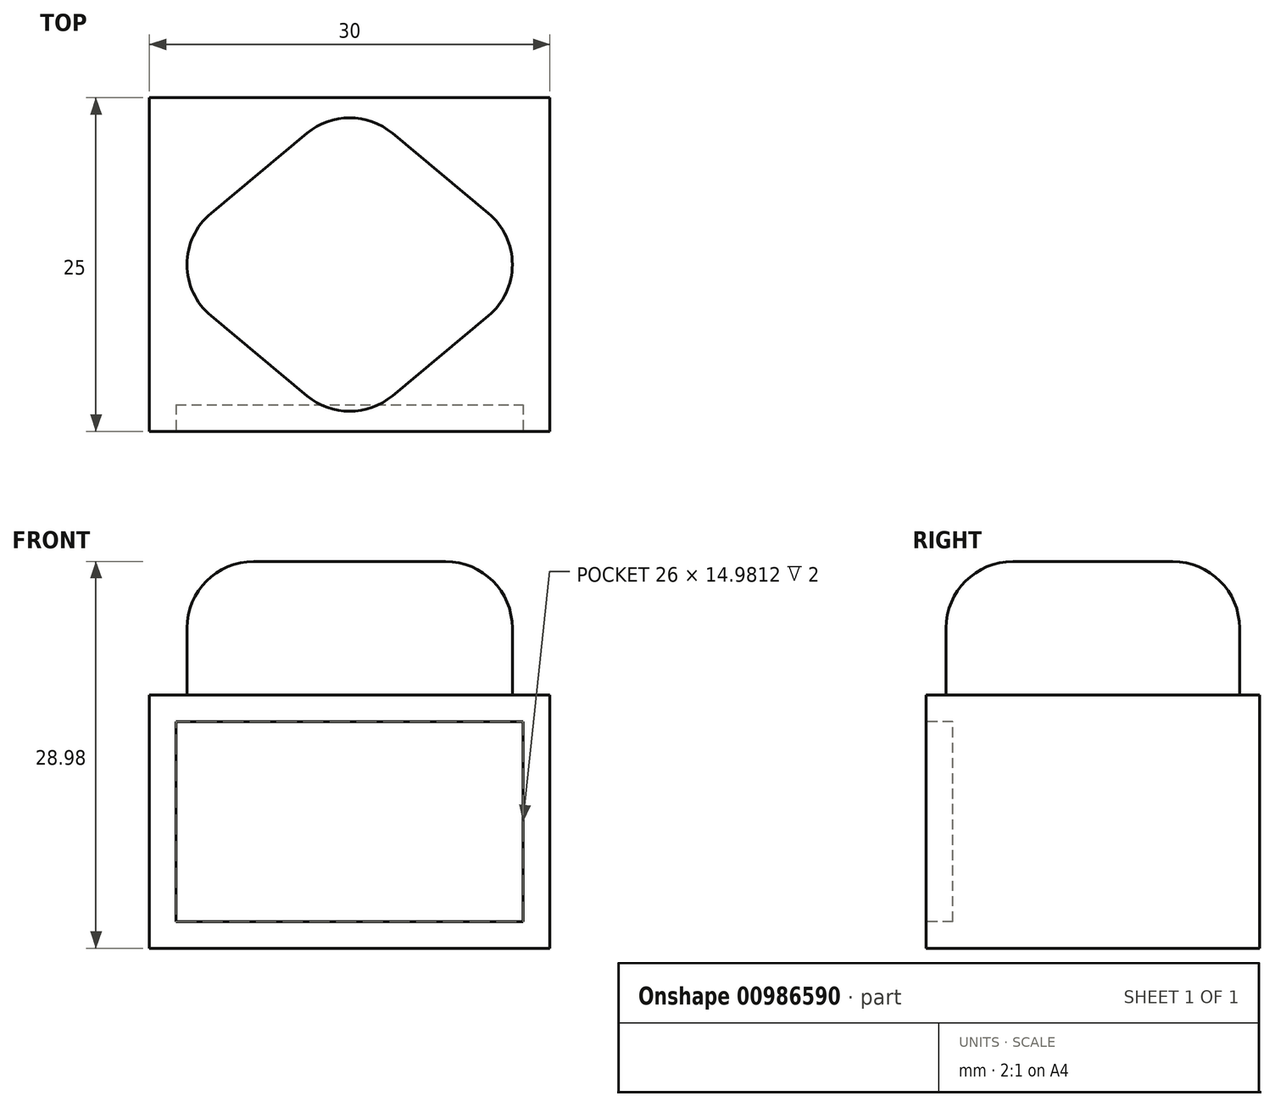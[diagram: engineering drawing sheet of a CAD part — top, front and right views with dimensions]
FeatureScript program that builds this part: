
annotation { "Feature Type Name" : "Feature", "Feature Type Description" : "" }
export const myFeature = defineFeature(function(context is Context, id is Id, definition is map)
    precondition{}
    {
        {
            var Q0;
            Q0=qCreatedBy(makeId("Front.planeOp"),FACE);
            var sketch = newSketch(context, id + "F0", { "sketchPlane" : qUnion([Q0])});
            skLineSegment(sketch, "E0.bottom", {"start": v(0, 0) * mm, "end": v(30, 0) * mm});
            skLineSegment(sketch, "E0.top", {"start": v(0, 18.98) * mm, "end": v(30, 18.98) * mm});
            skLineSegment(sketch, "E0.left", {"start": v(0, 0) * mm, "end": v(0, 18.98) * mm});
            skLineSegment(sketch, "E0.right", {"start": v(30, 0) * mm, "end": v(30, 18.98) * mm});
            skSolve(sketch);
        }
        {
            var Q0;
            Q0 = qSketchRegion(id + "F0", true);
            extrude(context, id + "F1", {"entities" : qUnion([Q0]), "endBound" : BoundingType.SYMMETRIC, "oppositeDirection" : true, "depth" : 25 * mm, "offsetDistance" : 25 * mm});
        }
        {
            var Q0;
            Q0=makeQuery(id+"F1.opExtrude","SWEPT_FACE",FACE,{"disambiguationData":[OSD([sQuery(id+"F0.wireOp",EDGE,"E0.top")])]});
            var sketch = newSketch(context, id + "F2", { "sketchPlane" : qUnion([Q0])});
            skLineSegment(sketch, "E1", {"start": v(0, 0) * mm, "end": v(15, 12.5) * mm});
            skLineSegment(sketch, "E2", {"start": v(15, 12.5) * mm, "end": v(30, 0) * mm});
            skLineSegment(sketch, "E3", {"start": v(30, 0) * mm, "end": v(15, -12.5) * mm});
            skLineSegment(sketch, "E4", {"start": v(15, -12.5) * mm, "end": v(0, 0) * mm});
            skLineSegment(sketch, "E5.0", {"start": v(-3.2, 3.84) * mm, "end": v(11.8, 16.34) * mm});
            skSolve(sketch);
        }
        {
            var Q0;
            Q0 = qSketchRegion(id + "F2", true);
            extrude(context, id + "F3", {"entities" : qUnion([Q0]), "operationType" : NewBodyOperationType.ADD, "depth" : 10 * mm, "offsetDistance" : 25 * mm});
        }
        {
            var Q0;
            Q0=makeQuery(id+"F3.opExtrude","CAP_FACE",FACE,{"disambiguationData":[OSD([sQuery(id+"F2.wireOp",EDGE,"E1"),sQuery(id+"F2.wireOp",EDGE,"E2"),sQuery(id+"F2.wireOp",EDGE,"E3"),sQuery(id+"F2.wireOp",EDGE,"E4")])],"isStart":false});
            var Q1;
            Q1=makeQuery(id+"F3.opExtrude","SWEPT_EDGE",EDGE,{"disambiguationData":[OSD([sQuery(id+"F0.wireOp",EDGE,"E0.top"),sQuery(id+"F2.wireOp",EDGE,"E3"),sQuery(id+"F2.wireOp",EDGE,"E4")])]});
            var Q2;
            Q2=makeQuery(id+"F3.opExtrude","SWEPT_EDGE",EDGE,{"disambiguationData":[OSD([sQuery(id+"F0.wireOp",EDGE,"E0.top"),sQuery(id+"F0.wireOp",EDGE,"E0.right"),sQuery(id+"F2.wireOp",EDGE,"E2"),sQuery(id+"F2.wireOp",EDGE,"E3")])]});
            var Q3;
            Q3=makeQuery(id+"F3.opExtrude","SWEPT_EDGE",EDGE,{"disambiguationData":[OSD([sQuery(id+"F0.wireOp",EDGE,"E0.top"),sQuery(id+"F2.wireOp",EDGE,"E1"),sQuery(id+"F2.wireOp",EDGE,"E2")])]});
            var Q4;
            Q4=makeQuery(id+"F3.opExtrude","SWEPT_EDGE",EDGE,{"disambiguationData":[OSD([sQuery(id+"F0.wireOp",EDGE,"E0.top"),sQuery(id+"F0.wireOp",EDGE,"E0.left"),sQuery(id+"F2.wireOp",EDGE,"E1"),sQuery(id+"F2.wireOp",EDGE,"E4")])]});
            fillet(context, id + "F4", {"entities" : qUnion([Q0, Q1, Q2, Q3, Q4]), "radius" : 5 * mm, "tangentPropagation" : true, "allowEdgeOverflow" : false});
        }
        {
            var Q0;
            Q0=makeQuery(id+"F1.opExtrude","CAP_FACE",FACE,{"disambiguationData":[OSD([sQuery(id+"F0.wireOp",EDGE,"E0.bottom"),sQuery(id+"F0.wireOp",EDGE,"E0.top"),sQuery(id+"F0.wireOp",EDGE,"E0.left"),sQuery(id+"F0.wireOp",EDGE,"E0.right")])],"isStart":true});
            var sketch = newSketch(context, id + "F5", { "sketchPlane" : qUnion([Q0])});
            skLineSegment(sketch, "E6.0", {"start": v(2, 16.98) * mm, "end": v(15, 16.98) * mm});
            skLineSegment(sketch, "E6.1", {"start": v(2, 2) * mm, "end": v(2, 16.98) * mm});
            skLineSegment(sketch, "E6.2", {"start": v(15, 16.98) * mm, "end": v(28, 16.98) * mm});
            skLineSegment(sketch, "E6.3", {"start": v(28, 2) * mm, "end": v(28, 16.98) * mm});
            skLineSegment(sketch, "E6.4", {"start": v(2, 2) * mm, "end": v(28, 2) * mm});
            skSolve(sketch);
        }
        {
            var Q0;
            Q0=makeQuery(id+"F5.imprint","IMPRINT",FACE,{"disambiguationData":[TD([[makeQuery(id+"F5.imprint","IMPRINT",EDGE,{"derivedFrom":sQuery(id+"F5.wireOp",EDGE,"E6.0")}),-1.0]])]});
            extrude(context, id + "F6", {"entities" : qUnion([Q0]), "operationType" : NewBodyOperationType.REMOVE, "oppositeDirection" : true, "depth" : 2 * mm, "offsetDistance" : 25 * mm});
        }
    });
